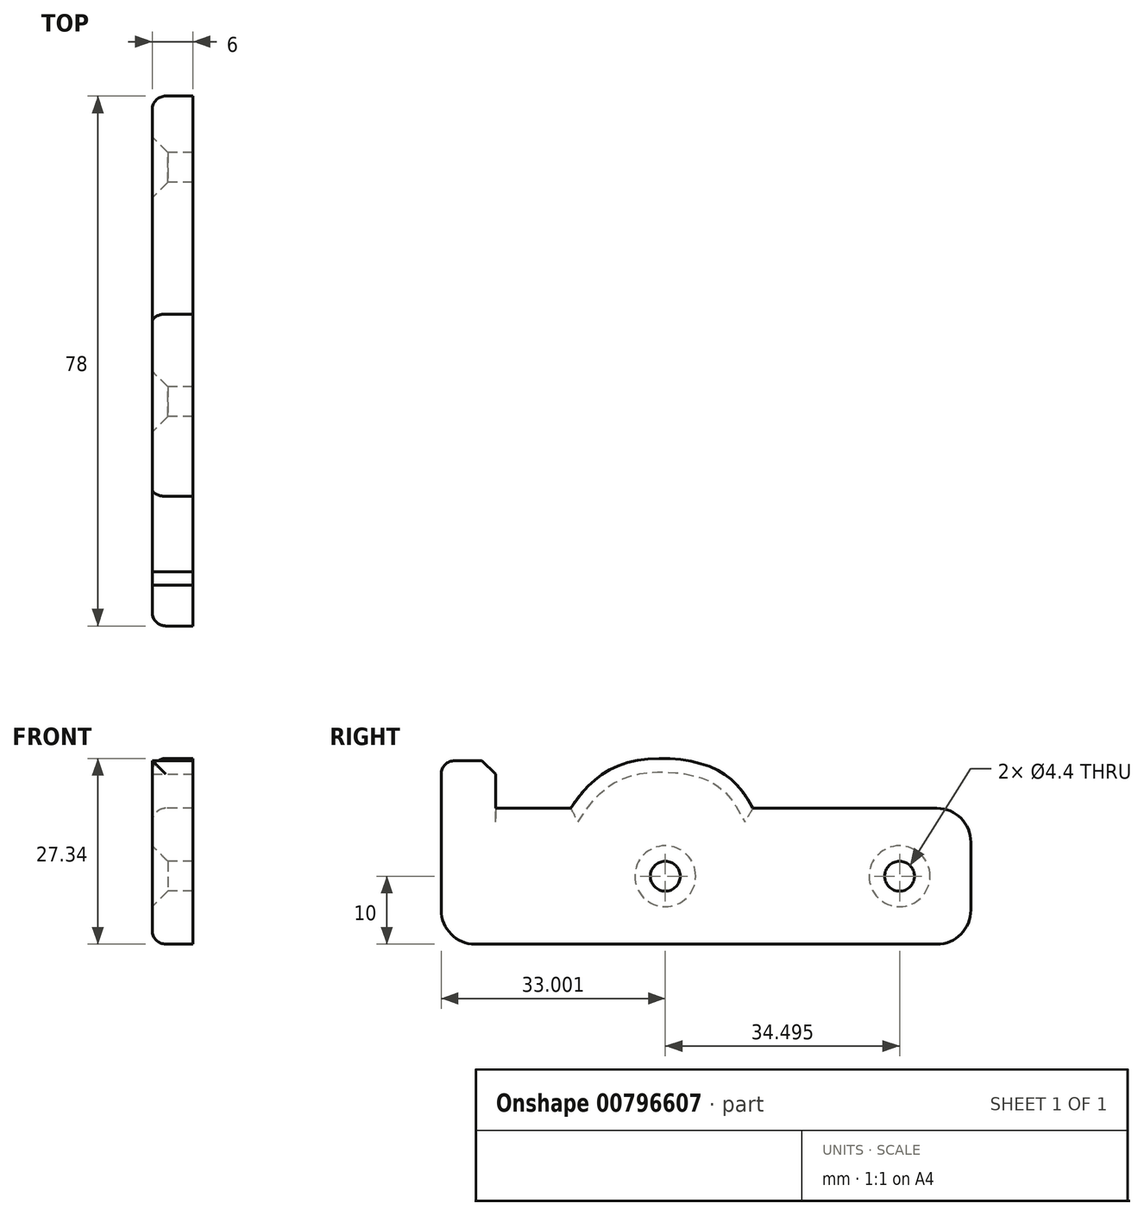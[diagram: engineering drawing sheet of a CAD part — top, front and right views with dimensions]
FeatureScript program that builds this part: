
annotation { "Feature Type Name" : "Feature", "Feature Type Description" : "" }
export const myFeature = defineFeature(function(context is Context, id is Id, definition is map)
    precondition{}
    {
        {
            var Q0;
            Q0=qCreatedBy(makeId("Right.planeOp"),FACE);
            var sketch = newSketch(context, id + "F0", { "sketchPlane" : qUnion([Q0])});
            skLineSegment(sketch, "E0", {"start": v(38.54, 0) * mm, "end": v(38.54, 20) * mm});
            skLineSegment(sketch, "E1", {"start": v(38.54, 20) * mm, "end": v(-31.46, 20) * mm});
            skLineSegment(sketch, "E2", {"start": v(-31.46, 20) * mm, "end": v(-31.46, 27) * mm});
            skLineSegment(sketch, "E3", {"start": v(-31.46, 27) * mm, "end": v(-39.46, 27) * mm});
            skLineSegment(sketch, "E4", {"start": v(-39.46, 27) * mm, "end": v(-39.46, 0) * mm});
            skLineSegment(sketch, "E5", {"start": v(-39.46, 0) * mm, "end": v(38.54, 0) * mm});
            skFitSpline(sketch, "E6", {"points": [v(-20.39, 20) * mm, v(-12.73, 26.5) * mm, v(0, 26.18) * mm, v(6.44, 20) * mm], "startDerivative": vector(18.04, 27.38) * mm, "endDerivative": vector(17.27, -31.3) * mm});
            skSolve(sketch);
        }
        {
            var Q0;
            Q0=makeQuery(id+"F0.imprint","IMPRINT",FACE,{"disambiguationData":[TD([[makeQuery(id+"F0.imprint","IMPRINT",EDGE,{"derivedFrom":sQuery(id+"F0.wireOp",EDGE,"E0")}),1.0]])]});
            var Q1;
            {var subQ0=sQuery(id+"F0.wireOp",EDGE,"E6");Q1=makeQuery(id+"F0.imprint","IMPRINT",FACE,{"disambiguationData":[TD([[makeQuery(id+"F0.imprint","IMPRINT",EDGE,{"derivedFrom":subQ0}),-1.0]])]});}
            extrude(context, id + "F1", {"entities" : qUnion([Q0, Q1]), "depth" : 6 * mm, "offsetDistance" : 25 * mm});
        }
        {
            var Q0;
            Q0=makeQuery(id+"F1.opExtrude","SWEPT_EDGE",EDGE,{"disambiguationData":[OSD([sQuery(id+"F0.wireOp",EDGE,"E0"),sQuery(id+"F0.wireOp",EDGE,"E1")])]});
            var Q1;
            Q1=makeQuery(id+"F1.opExtrude","SWEPT_EDGE",EDGE,{"disambiguationData":[OSD([sQuery(id+"F0.wireOp",EDGE,"E0"),sQuery(id+"F0.wireOp",EDGE,"E5")])]});
            var Q2;
            Q2=makeQuery(id+"F1.opExtrude","SWEPT_EDGE",EDGE,{"disambiguationData":[OSD([sQuery(id+"F0.wireOp",EDGE,"E4"),sQuery(id+"F0.wireOp",EDGE,"E5")])]});
            fillet(context, id + "F2", {"entities" : qUnion([Q0, Q1, Q2]), "radius" : 5 * mm, "tangentPropagation" : true, "allowEdgeOverflow" : false});
        }
        {
            var Q0;
            Q0=makeQuery(id+"F1.opExtrude","CAP_EDGE",EDGE,{"disambiguationData":[OSD([sQuery(id+"F0.wireOp",EDGE,"E1")])],"isStart":true});
            var Q1;
            Q1=makeQuery(id+"F1.opExtrude","SWEPT_EDGE",EDGE,{"disambiguationData":[OSD([sQuery(id+"F0.wireOp",EDGE,"E3"),sQuery(id+"F0.wireOp",EDGE,"E4")])]});
            var Q2;
            Q2=makeQuery(id+"F1.opExtrude","CAP_EDGE",EDGE,{"disambiguationData":[OSD([sQuery(id+"F0.wireOp",EDGE,"E6")])],"isStart":true});
            fillet(context, id + "F3", {"entities" : qUnion([Q0, Q1, Q2]), "radius" : 2 * mm, "tangentPropagation" : true, "allowEdgeOverflow" : false});
        }
        {
            var Q0;
            Q0=makeQuery(id+"F1.opExtrude","CAP_FACE",FACE,{"disambiguationData":[OSD([sQuery(id+"F0.wireOp",EDGE,"E0"),sQuery(id+"F0.wireOp",EDGE,"E1"),sQuery(id+"F0.wireOp",EDGE,"E2"),sQuery(id+"F0.wireOp",EDGE,"E3"),sQuery(id+"F0.wireOp",EDGE,"E4"),sQuery(id+"F0.wireOp",EDGE,"E5")])],"isStart":true});
            var sketch = newSketch(context, id + "F4", { "sketchPlane" : qUnion([Q0])});
            skPoint(sketch, "E7", {"position": v(-28.04, 10) * mm});
            skPoint(sketch, "E7.positionSnap0", {"position": v(-36.54, 10) * mm});
            skPoint(sketch, "E8", {"position": v(6.46, 10) * mm});
            skSolve(sketch);
        }
        {
            var Q0;
            Q0=sQuery(id+"F4.wireOp",VERTEX,"E7");
            var Q1;
            Q1=sQuery(id+"F4.wireOp",VERTEX,"321f2fa2-082a-4344-a82a-c2016e4dd672");
            var Q2;
            Q2=sQuery(id+"F4.wireOp",VERTEX,"E8");
            var Q3;
            Q3=makeQuery(id+"F1.opExtrude","SWEPT_BODY",BODY,{"disambiguationData":[OSD([sQuery(id+"F0.wireOp",EDGE,"E0"),sQuery(id+"F0.wireOp",EDGE,"E1"),sQuery(id+"F0.wireOp",EDGE,"E2"),sQuery(id+"F0.wireOp",EDGE,"E3"),sQuery(id+"F0.wireOp",EDGE,"E4"),sQuery(id+"F0.wireOp",EDGE,"E5")])]});
            hole(context, id + "F5", {"style" : HoleStyle.C_SINK, "endStyle" : HoleEndStyle.THROUGH, "standardTappedOrClearance" : lookupTablePath({ "standard" : "ISO", "fit" : "Normal", "size" : "M4", "type" : "Clearance" }), "standardBlindInLast" : lookupTablePath({ "fit" : "Standard", "standard" : "ISO", "size" : "M4", "type" : "Clearance" }), "holeDiameter" : 4.4 * mm, "cSinkDiameter" : 8.96 * mm, "cSinkAngle" : 90 * degree, "majorDiameter" : 5 * mm, "isTappedThrough" : true, "tappedDepth" : 12 * mm, "tapClearance" : 3, "locations" : qUnion([Q0, Q1, Q2]), "scope" : qUnion([Q3])});
        }
        {
            var Q0;
            Q0=makeQuery(id+"F1.opExtrude","SWEPT_EDGE",EDGE,{"disambiguationData":[OSD([sQuery(id+"F0.wireOp",EDGE,"E2"),sQuery(id+"F0.wireOp",EDGE,"E3")])]});
            chamfer(context, id + "F6", {"entities" : qUnion([Q0]), "width" : 2 * mm, "tangentPropagation" : true});
        }
    });
